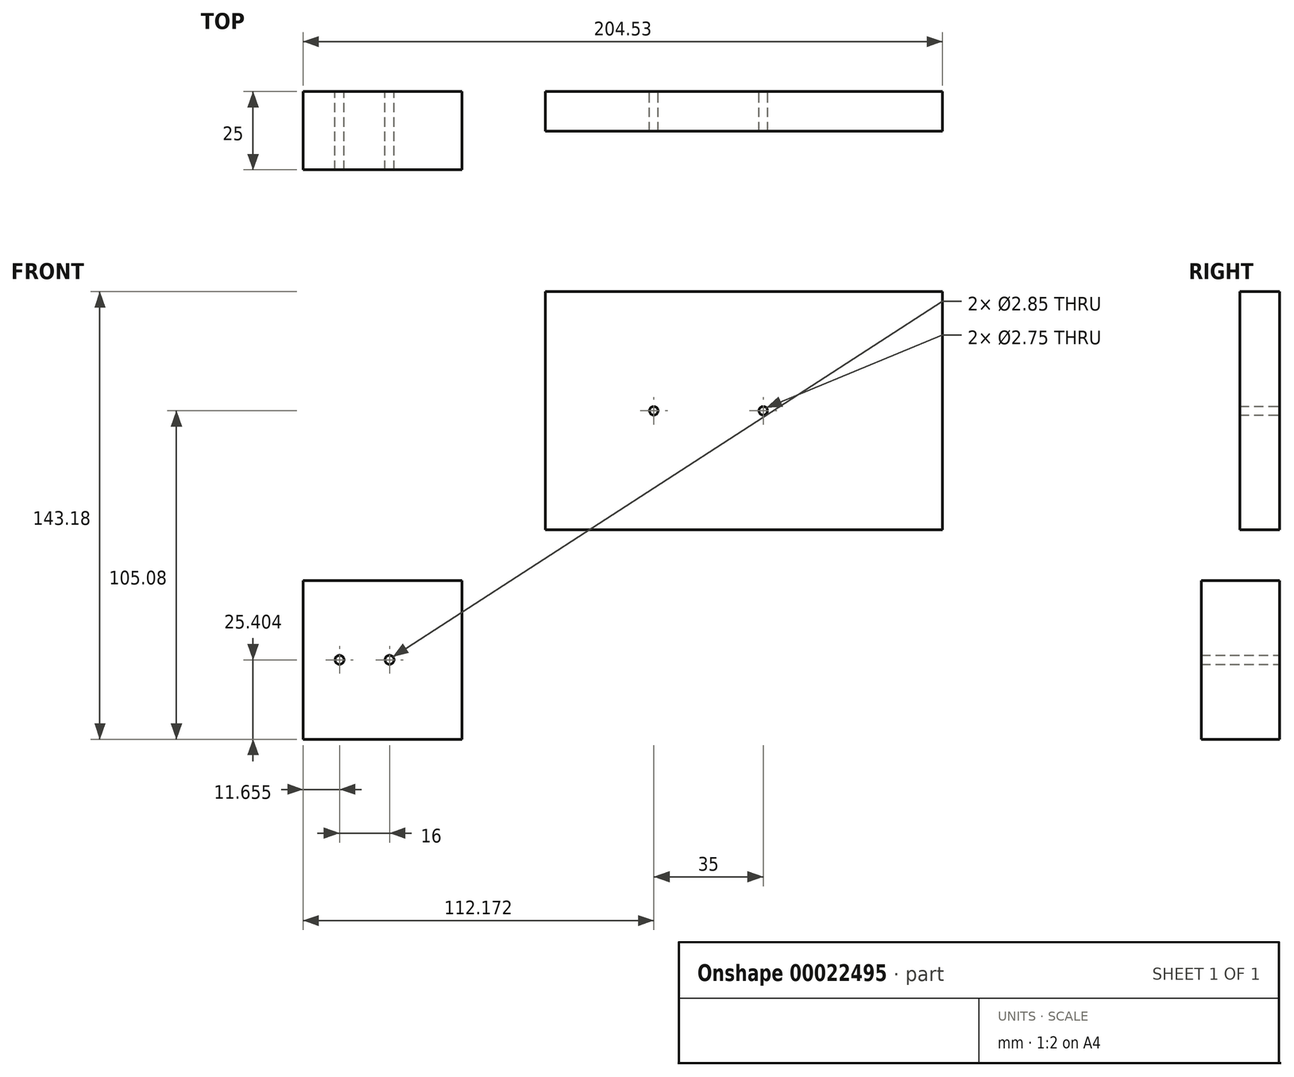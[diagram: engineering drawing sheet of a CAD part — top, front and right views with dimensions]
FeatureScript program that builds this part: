
annotation { "Feature Type Name" : "Feature", "Feature Type Description" : "" }
export const myFeature = defineFeature(function(context is Context, id is Id, definition is map)
    precondition{}
    {
        {
            var Q0;
            Q0=qCreatedBy(makeId("Front.planeOp"),FACE);
            var sketch = newSketch(context, id + "F0", { "sketchPlane" : qUnion([Q0])});
            skLineSegment(sketch, "E0.bottom", {"start": v(-67.31, 38.05) * mm, "end": v(59.69, 38.05) * mm});
            skLineSegment(sketch, "E0.top", {"start": v(-67.31, -38.15) * mm, "end": v(59.69, -38.15) * mm});
            skLineSegment(sketch, "E0.left", {"start": v(-67.31, 38.05) * mm, "end": v(-67.31, -38.15) * mm});
            skLineSegment(sketch, "E0.right", {"start": v(59.69, 38.05) * mm, "end": v(59.69, -38.15) * mm});
            skLineSegment(sketch, "E1", {"start": v(-67.31, -0.05) * mm, "end": v(59.69, -0.05) * mm});
            skCircle(sketch, "E2", {"center": v(-32.67, -0.05) * mm, "radius": 1.38 * mm});
            skCircle(sketch, "E3", {"center": v(2.33, -0.05) * mm, "radius": 1.38 * mm});
            skSolve(sketch);
        }
        {
            var Q0;
            Q0 = qSketchRegion(id + "F0", true);
            var Q1;
            Q1=makeQuery(id+"F0.imprint","IMPRINT",FACE,{"disambiguationData":[TD([[makeQuery(id+"F0.imprint","IMPRINT",EDGE,{"derivedFrom":sQuery(id+"F0.wireOp",EDGE,"E0.bottom")}),-1.0]])]});
            extrude(context, id + "F1", {"entities" : qUnion([Q0, Q1]), "depth" : 12.7 * mm});
        }
        {
            var Q0;
            Q0=qCreatedBy(makeId("Front.planeOp"),FACE);
            var sketch = newSketch(context, id + "F2", { "sketchPlane" : qUnion([Q0])});
            skLineSegment(sketch, "E4.bottom", {"start": v(-144.84, -54.33) * mm, "end": v(-94.04, -54.33) * mm});
            skLineSegment(sketch, "E4.top", {"start": v(-144.84, -105.13) * mm, "end": v(-94.04, -105.13) * mm});
            skLineSegment(sketch, "E4.left", {"start": v(-144.84, -54.33) * mm, "end": v(-144.84, -105.13) * mm});
            skLineSegment(sketch, "E4.right", {"start": v(-94.04, -54.33) * mm, "end": v(-94.04, -105.13) * mm});
            skLineSegment(sketch, "E5", {"start": v(-144.84, -79.73) * mm, "end": v(-94.04, -79.73) * mm});
            skCircle(sketch, "E6", {"center": v(-133.18, -79.73) * mm, "radius": 1.43 * mm});
            skCircle(sketch, "E7", {"center": v(-117.18, -79.73) * mm, "radius": 1.43 * mm});
            skSolve(sketch);
        }
        {
            var Q0;
            Q0=makeQuery(id+"F2.imprint","IMPRINT",FACE,{"disambiguationData":[TD([[makeQuery(id+"F2.imprint","IMPRINT",EDGE,{"derivedFrom":sQuery(id+"F2.wireOp",EDGE,"E4.bottom")}),-1.0]])]});
            extrude(context, id + "F3", {"entities" : qUnion([Q0]), "depth" : 12.7 * mm});
        }
        {
            var Q0;
            Q0 = qSketchRegion(id + "F0", true);
            extrude(context, id + "F4", {"entities" : qUnion([Q0]), "operationType" : NewBodyOperationType.REMOVE, "oppositeDirection" : true, "depth" : 25 * mm});
        }
        {
            var Q0;
            Q0 = qSketchRegion(id + "F2", true);
            extrude(context, id + "F5", {"entities" : qUnion([Q0]), "operationType" : NewBodyOperationType.ADD, "depth" : 25 * mm});
        }
    });
